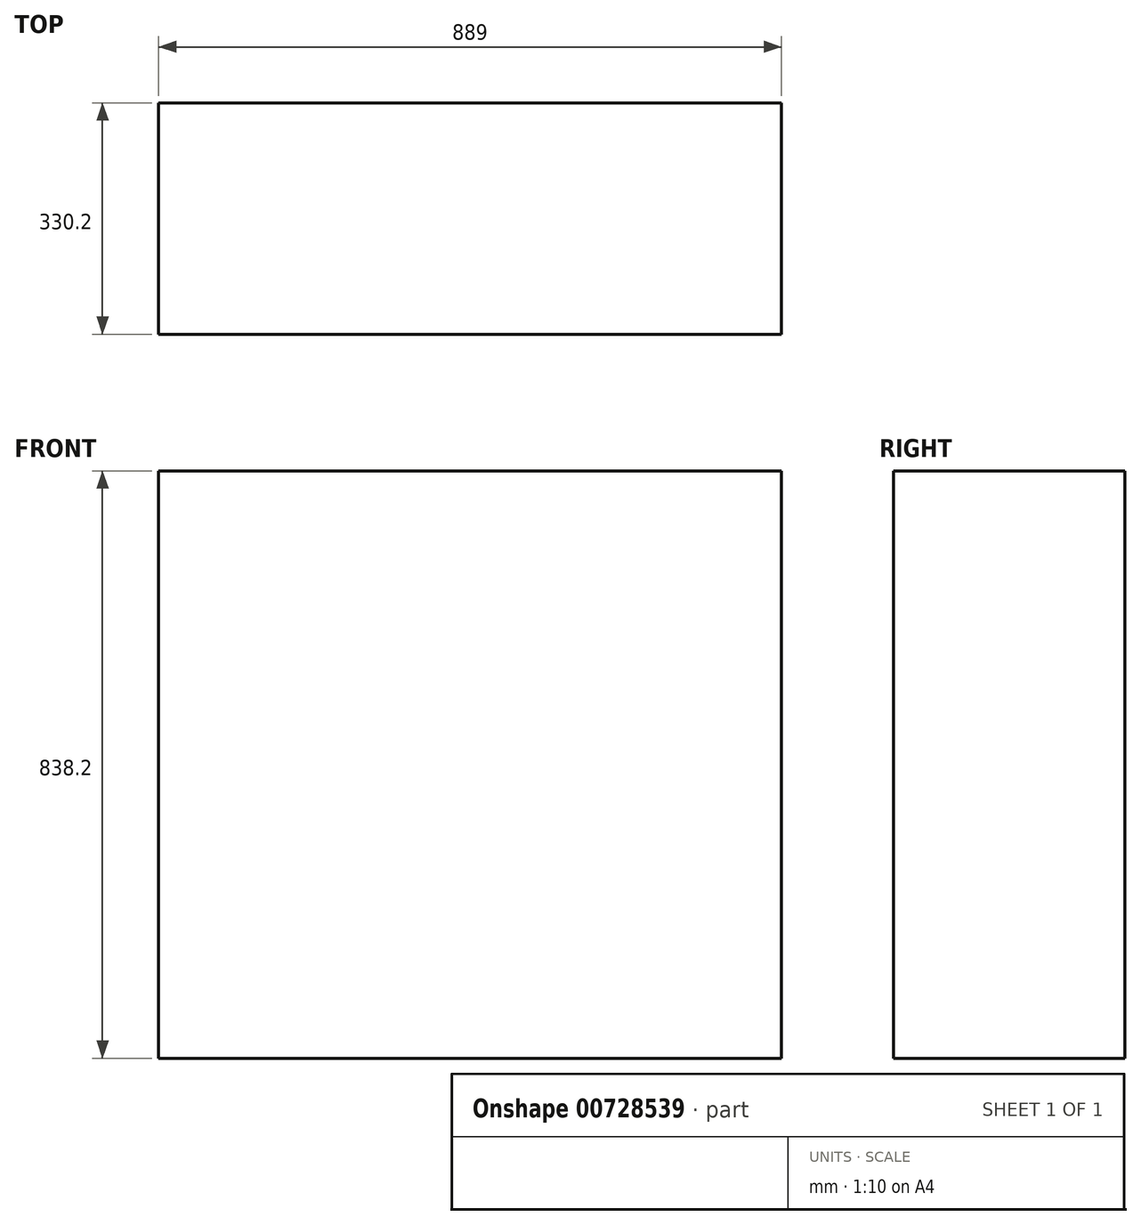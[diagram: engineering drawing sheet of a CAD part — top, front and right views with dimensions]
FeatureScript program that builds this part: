
annotation { "Feature Type Name" : "Feature", "Feature Type Description" : "" }
export const myFeature = defineFeature(function(context is Context, id is Id, definition is map)
    precondition{}
    {
        {
            var Q0;
            Q0=qCreatedBy(makeId("Top.planeOp"),FACE);
            var sketch = newSketch(context, id + "F0", { "sketchPlane" : qUnion([Q0])});
            skLineSegment(sketch, "E0.bottom", {"start": v(444.5, 165.1) * mm, "end": v(-444.5, 165.1) * mm});
            skLineSegment(sketch, "E0.top", {"start": v(444.5, -165.1) * mm, "end": v(-444.5, -165.1) * mm});
            skLineSegment(sketch, "E0.left", {"start": v(444.5, 165.1) * mm, "end": v(444.5, -165.1) * mm});
            skLineSegment(sketch, "E0.right", {"start": v(-444.5, 165.1) * mm, "end": v(-444.5, -165.1) * mm});
            skPoint(sketch, "E0.middle", {"position": v(0, 0) * mm});
            skSolve(sketch);
        }
        {
            var Q0;
            Q0 = qSketchRegion(id + "F0", true);
            extrude(context, id + "F1", {"entities" : qUnion([Q0]), "depth" : 838.2 * mm, "offsetDistance" : 25.4 * mm});
        }
    });
